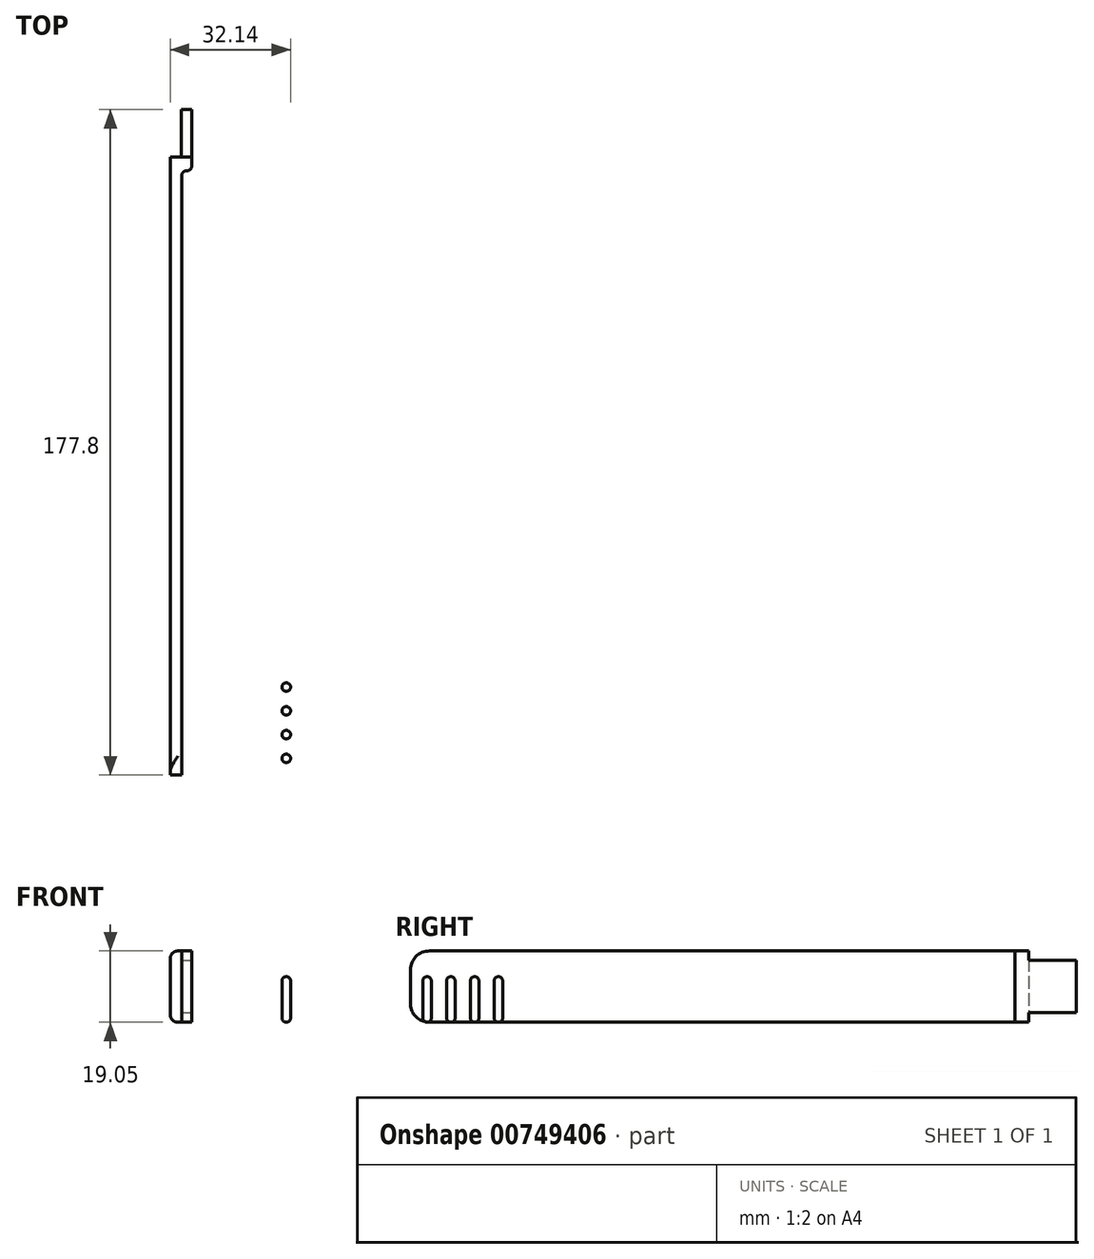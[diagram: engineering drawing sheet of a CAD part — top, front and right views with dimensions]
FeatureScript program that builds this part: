
annotation { "Feature Type Name" : "Feature", "Feature Type Description" : "" }
export const myFeature = defineFeature(function(context is Context, id is Id, definition is map)
    precondition{}
    {
        {
            var Q0;
            Q0=qCreatedBy(makeId("Top.planeOp"),FACE);
            var sketch = newSketch(context, id + "F0", { "sketchPlane" : qUnion([Q0])});
            skLineSegment(sketch, "E0", {"start": v(0, 0) * mm, "end": v(0, 165.1) * mm});
            skLineSegment(sketch, "E1", {"start": v(0, 165.1) * mm, "end": v(2.92, 165.1) * mm});
            skLineSegment(sketch, "E2", {"start": v(2.92, 165.1) * mm, "end": v(2.92, 177.8) * mm});
            skLineSegment(sketch, "E3", {"start": v(2.92, 177.8) * mm, "end": v(5.71, 177.8) * mm});
            skLineSegment(sketch, "E4", {"start": v(3.05, 0) * mm, "end": v(0, 0) * mm});
            skLineSegment(sketch, "E5", {"start": v(5.71, 177.8) * mm, "end": v(5.71, 161.45) * mm});
            skLineSegment(sketch, "E6", {"start": v(3.05, 161.45) * mm, "end": v(3.05, 0) * mm});
            skLineSegment(sketch, "E7", {"start": v(3.05, 161.45) * mm, "end": v(5.71, 161.45) * mm});
            skSolve(sketch);
        }
        {
            var Q0;
            Q0=makeQuery(id+"F0.imprint","IMPRINT",FACE,{"disambiguationData":[TD([[makeQuery(id+"F0.imprint","IMPRINT",EDGE,{"derivedFrom":sQuery(id+"F0.wireOp",EDGE,"E0")}),-1.0]])]});
            extrude(context, id + "F1", {"entities" : qUnion([Q0]), "depth" : 19.05 * mm, "offsetDistance" : 25.4 * mm});
        }
        {
            var Q0;
            Q0=makeQuery(id+"F1.opExtrude","CAP_EDGE",EDGE,{"disambiguationData":[OSD([sQuery(id+"F0.wireOp",EDGE,"E4")])],"isStart":false});
            fillet(context, id + "F2", {"entities" : qUnion([Q0]), "radius" : 5.08 * mm, "allowEdgeOverflow" : false});
        }
        {
            var Q0;
            Q0=makeQuery(id+"F1.opExtrude","CAP_EDGE",EDGE,{"disambiguationData":[OSD([sQuery(id+"F0.wireOp",EDGE,"E4")])],"isStart":true});
            fillet(context, id + "F3", {"entities" : qUnion([Q0]), "radius" : 5.08 * mm, "tangentPropagation" : true, "allowEdgeOverflow" : false});
        }
        {
            var Q0;
            Q0=makeQuery(id+"F1.opExtrude","SWEPT_EDGE",EDGE,{"disambiguationData":[OSD([sQuery(id+"F0.wireOp",EDGE,"E5"),sQuery(id+"F0.wireOp",EDGE,"E7")])]});
            var Q1;
            Q1=makeQuery(id+"F1.opExtrude","SWEPT_EDGE",EDGE,{"disambiguationData":[OSD([sQuery(id+"F0.wireOp",EDGE,"E6"),sQuery(id+"F0.wireOp",EDGE,"E7")])]});
            fillet(context, id + "F4", {"entities" : qUnion([Q0, Q1]), "radius" : 1.27 * mm, "tangentPropagation" : true, "allowEdgeOverflow" : false});
        }
        {
            var Q0;
            Q0=makeQuery(id+"F1.opExtrude","CAP_EDGE",EDGE,{"disambiguationData":[OSD([sQuery(id+"F0.wireOp",EDGE,"E0")])],"isStart":false});
            var Q1;
            Q1=makeQuery(id+"F1.opExtrude","CAP_EDGE",EDGE,{"disambiguationData":[OSD([sQuery(id+"F0.wireOp",EDGE,"E0")])],"isStart":true});
            fillet(context, id + "F5", {"entities" : qUnion([Q0, Q1]), "radius" : 2.03 * mm, "allowEdgeOverflow" : false});
        }
        {
            var Q0;
            Q0=makeQuery(id+"F1.opExtrude","SWEPT_FACE",FACE,{"disambiguationData":[OSD([sQuery(id+"F0.wireOp",EDGE,"E5")])]});
            var sketch = newSketch(context, id + "F6", { "sketchPlane" : qUnion([Q0])});
            skLineSegment(sketch, "E8", {"start": v(177.8, 19.05) * mm, "end": v(177.8, 16.51) * mm});
            skLineSegment(sketch, "E9", {"start": v(177.8, 16.51) * mm, "end": v(165.1, 16.51) * mm});
            skLineSegment(sketch, "E10", {"start": v(165.1, 16.51) * mm, "end": v(165.1, 19.05) * mm});
            skLineSegment(sketch, "E11", {"start": v(165.1, 19.05) * mm, "end": v(177.8, 19.05) * mm});
            skLineSegment(sketch, "E12", {"start": v(177.8, 0) * mm, "end": v(177.8, 2.54) * mm});
            skLineSegment(sketch, "E13", {"start": v(177.8, 2.54) * mm, "end": v(165.1, 2.54) * mm});
            skLineSegment(sketch, "E14", {"start": v(165.1, 2.54) * mm, "end": v(165.1, 0) * mm});
            skLineSegment(sketch, "E15", {"start": v(165.1, 0) * mm, "end": v(177.8, 0) * mm});
            skSolve(sketch);
        }
        {
            var Q0;
            Q0=makeQuery(id+"F6.imprint","IMPRINT",FACE,{"disambiguationData":[TD([[makeQuery(id+"F6.imprint","IMPRINT",EDGE,{"derivedFrom":sQuery(id+"F6.wireOp",EDGE,"E8")}),-1.0]])]});
            extrude(context, id + "F7", {"entities" : qUnion([Q0]), "operationType" : NewBodyOperationType.REMOVE, "oppositeDirection" : true, "depth" : 25.4 * mm, "offsetDistance" : 25.4 * mm});
        }
        {
            var Q0;
            Q0=makeQuery(id+"F1.opExtrude","SWEPT_FACE",FACE,{"disambiguationData":[OSD([sQuery(id+"F0.wireOp",EDGE,"E5")])]});
            var sketch = newSketch(context, id + "F8", { "sketchPlane" : qUnion([Q0])});
            skLineSegment(sketch, "E16", {"start": v(177.8, 0) * mm, "end": v(177.8, 2.54) * mm});
            skLineSegment(sketch, "E17", {"start": v(177.8, 2.54) * mm, "end": v(165.1, 2.54) * mm});
            skLineSegment(sketch, "E18", {"start": v(165.1, 2.54) * mm, "end": v(165.1, 0) * mm});
            skLineSegment(sketch, "E19", {"start": v(165.1, 0) * mm, "end": v(177.8, 0) * mm});
            skSolve(sketch);
        }
        {
            var Q0;
            Q0=makeQuery(id+"F8.imprint","IMPRINT",FACE,{"disambiguationData":[TD([[makeQuery(id+"F8.imprint","IMPRINT",EDGE,{"derivedFrom":sQuery(id+"F8.wireOp",EDGE,"E16")}),-1.0]])]});
            extrude(context, id + "F9", {"entities" : qUnion([Q0]), "operationType" : NewBodyOperationType.REMOVE, "oppositeDirection" : true, "depth" : 25.4 * mm, "offsetDistance" : 25.4 * mm});
        }
        {
            var Q0;
            Q0=qCreatedBy(makeId("Top.planeOp"),FACE);
            var sketch = newSketch(context, id + "F10", { "sketchPlane" : qUnion([Q0])});
            skCircle(sketch, "E20", {"center": v(31, 4.46) * mm, "radius": 1.14 * mm});
            skLineSegment(sketch, "E21.direction1", {"start": v(31, 4.46) * mm, "end": v(56.4, 4.46) * mm, "construction": true});
            skLineSegment(sketch, "E21.direction2", {"start": v(31, 4.46) * mm, "end": v(31, 10.8) * mm, "construction": true});
            skCircle(sketch, "E22.0.0.1", {"center": v(31, 10.8) * mm, "radius": 1.14 * mm});
            skCircle(sketch, "E22.0.0.2", {"center": v(31, 17.16) * mm, "radius": 1.14 * mm});
            skCircle(sketch, "E22.0.0.3", {"center": v(31, 23.5) * mm, "radius": 1.14 * mm});
            skSolve(sketch);
        }
        {
            var Q0;
            Q0=makeQuery(id+"F10.imprint","IMPRINT",FACE,{"disambiguationData":[TD([[makeQuery(id+"F10.imprint","IMPRINT",EDGE,{"derivedFrom":sQuery(id+"F10.wireOp",EDGE,"E20")}),1.0]])]});
            var Q1;
            Q1=makeQuery(id+"F10.imprint","IMPRINT",FACE,{"disambiguationData":[TD([[makeQuery(id+"F10.imprint","IMPRINT",EDGE,{"derivedFrom":sQuery(id+"F10.wireOp",EDGE,"E22.0.0.1")}),1.0]])]});
            var Q2;
            Q2=makeQuery(id+"F10.imprint","IMPRINT",FACE,{"disambiguationData":[TD([[makeQuery(id+"F10.imprint","IMPRINT",EDGE,{"derivedFrom":sQuery(id+"F10.wireOp",EDGE,"E22.0.0.2")}),1.0]])]});
            var Q3;
            Q3=makeQuery(id+"F10.imprint","IMPRINT",FACE,{"disambiguationData":[TD([[makeQuery(id+"F10.imprint","IMPRINT",EDGE,{"derivedFrom":sQuery(id+"F10.wireOp",EDGE,"E22.0.0.3")}),1.0]])]});
            extrude(context, id + "F11", {"entities" : qUnion([Q0, Q1, Q2, Q3]), "depth" : 12.2 * mm, "offsetDistance" : 25.4 * mm});
        }
        {
            var Q0;
            Q0=makeQuery(id+"F11.opExtrude","CAP_EDGE",EDGE,{"disambiguationData":[OSD([sQuery(id+"F10.wireOp",EDGE,"E20")])],"isStart":false});
            var Q1;
            Q1=makeQuery(id+"F11.opExtrude","CAP_EDGE",EDGE,{"disambiguationData":[OSD([sQuery(id+"F10.wireOp",EDGE,"E22.0.0.1")])],"isStart":false});
            var Q2;
            Q2=makeQuery(id+"F11.opExtrude","CAP_EDGE",EDGE,{"disambiguationData":[OSD([sQuery(id+"F10.wireOp",EDGE,"E22.0.0.2")])],"isStart":false});
            var Q3;
            Q3=makeQuery(id+"F11.opExtrude","CAP_EDGE",EDGE,{"disambiguationData":[OSD([sQuery(id+"F10.wireOp",EDGE,"E22.0.0.3")])],"isStart":false});
            var Q4;
            Q4=makeQuery(id+"F11.opExtrude","CAP_EDGE",EDGE,{"disambiguationData":[OSD([sQuery(id+"F10.wireOp",EDGE,"E22.0.0.3")])],"isStart":true});
            var Q5;
            Q5=makeQuery(id+"F11.opExtrude","CAP_EDGE",EDGE,{"disambiguationData":[OSD([sQuery(id+"F10.wireOp",EDGE,"E22.0.0.2")])],"isStart":true});
            var Q6;
            Q6=makeQuery(id+"F11.opExtrude","CAP_EDGE",EDGE,{"disambiguationData":[OSD([sQuery(id+"F10.wireOp",EDGE,"E22.0.0.1")])],"isStart":true});
            var Q7;
            Q7=makeQuery(id+"F11.opExtrude","CAP_EDGE",EDGE,{"disambiguationData":[OSD([sQuery(id+"F10.wireOp",EDGE,"E20")])],"isStart":true});
            fillet(context, id + "F12", {"entities" : qUnion([Q0, Q1, Q2, Q3, Q4, Q5, Q6, Q7]), "radius" : 1.14 * mm, "tangentPropagation" : true, "allowEdgeOverflow" : false});
        }
    });
